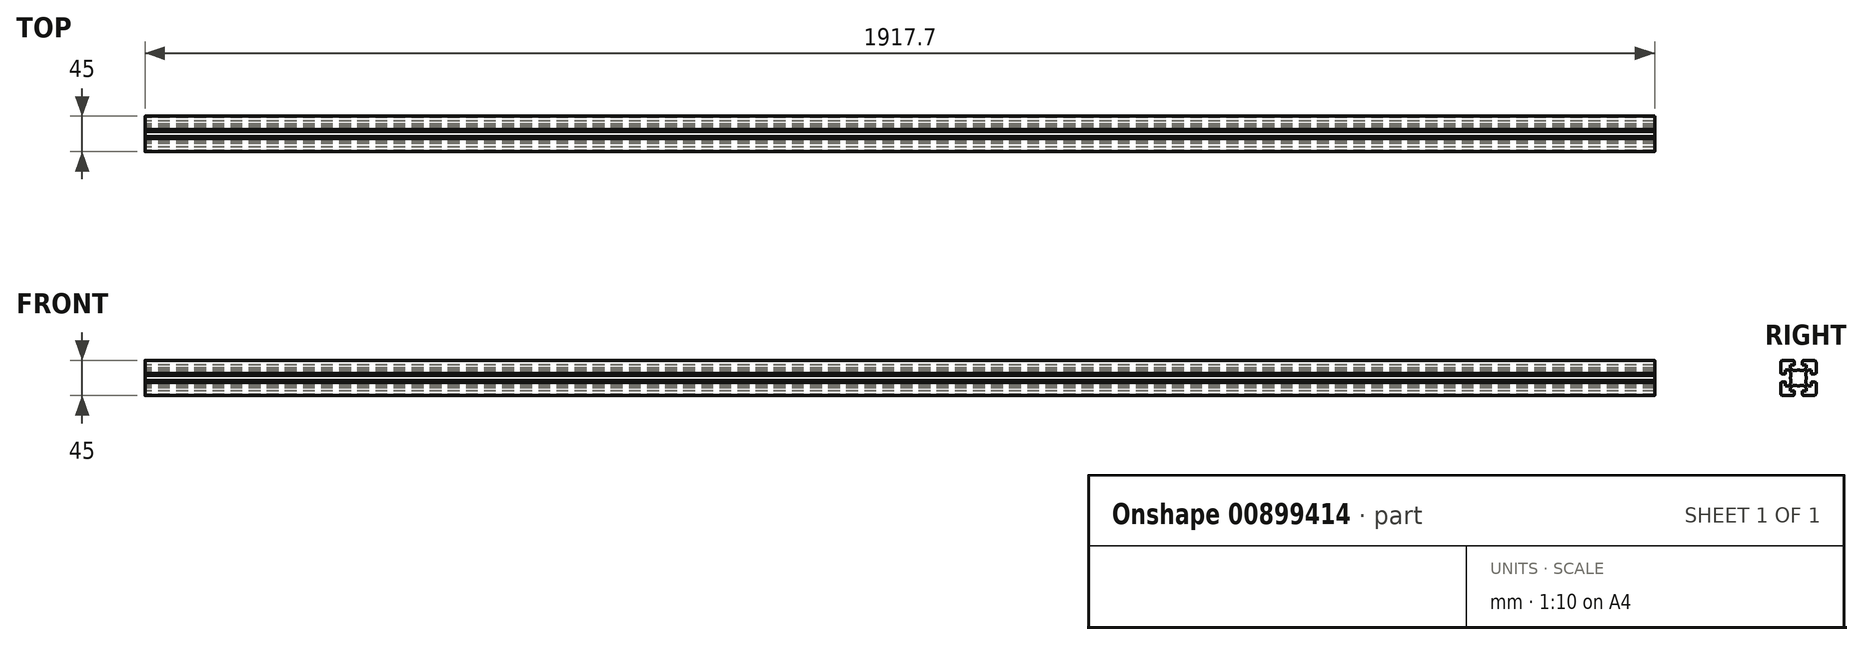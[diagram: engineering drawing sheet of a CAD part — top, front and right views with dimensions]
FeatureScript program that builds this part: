
annotation { "Feature Type Name" : "Feature", "Feature Type Description" : "" }
export const myFeature = defineFeature(function(context is Context, id is Id, definition is map)
    precondition{}
    {
        {
            var Q0;
            Q0=qCreatedBy(makeId("Right.planeOp"),FACE);
            var sketch = newSketch(context, id + "F0", { "sketchPlane" : qUnion([Q0])});
            skLineSegment(sketch, "E0", {"start": v(-20.09, -10.29) * mm, "end": v(-21.29, -10.29) * mm});
            skArc(sketch, "E1", {"start": v(-21.29, -10.29) * mm, "mid": v(-21.5, -10.38) * mm, "end": v(-21.59, -10.59) * mm});
            skLineSegment(sketch, "E2", {"start": v(-21.59, -10.59) * mm, "end": v(-21.59, -23.99) * mm});
            skArc(sketch, "E3", {"start": v(-21.59, -23.99) * mm, "mid": v(-20.7, -26.11) * mm, "end": v(-18.59, -26.99) * mm});
            skLineSegment(sketch, "E4", {"start": v(-18.59, -26.99) * mm, "end": v(-5.19, -26.99) * mm});
            skArc(sketch, "E5", {"start": v(-5.19, -26.99) * mm, "mid": v(-4.98, -26.9) * mm, "end": v(-4.89, -26.69) * mm});
            skLineSegment(sketch, "E6", {"start": v(-4.89, -26.69) * mm, "end": v(-4.89, -25.49) * mm});
            skLineSegment(sketch, "E7", {"start": v(-4.89, -25.49) * mm, "end": v(-4.39, -25.49) * mm});
            skArc(sketch, "E8", {"start": v(-4.39, -25.49) * mm, "mid": v(-4.18, -25.4) * mm, "end": v(-4.09, -25.19) * mm});
            skLineSegment(sketch, "E9", {"start": v(-4.09, -25.19) * mm, "end": v(-4.09, -21.29) * mm});
            skArc(sketch, "E10", {"start": v(-4.09, -21.29) * mm, "mid": v(-4.18, -21.08) * mm, "end": v(-4.39, -20.99) * mm});
            skLineSegment(sketch, "E11", {"start": v(-4.39, -20.99) * mm, "end": v(-9.14, -20.99) * mm});
            skLineSegment(sketch, "E12", {"start": v(-9.14, -20.99) * mm, "end": v(-9.14, -16.88) * mm});
            skLineSegment(sketch, "E13", {"start": v(-9.14, -16.88) * mm, "end": v(-6.25, -13.99) * mm});
            skLineSegment(sketch, "E14", {"start": v(-6.25, -13.99) * mm, "end": v(-2.21, -13.99) * mm});
            skArc(sketch, "E15", {"start": v(-2.21, -13.99) * mm, "mid": v(0.91, -14.49) * mm, "end": v(4.03, -13.99) * mm});
            skLineSegment(sketch, "E16", {"start": v(-20.09, -10.29) * mm, "end": v(-20.09, -9.79) * mm});
            skArc(sketch, "E17", {"start": v(-20.09, -9.79) * mm, "mid": v(-20, -9.58) * mm, "end": v(-19.79, -9.49) * mm});
            skLineSegment(sketch, "E18", {"start": v(-19.79, -9.49) * mm, "end": v(-15.89, -9.49) * mm});
            skArc(sketch, "E19", {"start": v(-15.89, -9.49) * mm, "mid": v(-15.68, -9.58) * mm, "end": v(-15.59, -9.79) * mm});
            skLineSegment(sketch, "E20", {"start": v(-15.59, -9.79) * mm, "end": v(-15.59, -14.54) * mm});
            skLineSegment(sketch, "E21", {"start": v(-15.59, -14.54) * mm, "end": v(-11.48, -14.54) * mm});
            skLineSegment(sketch, "E22", {"start": v(-11.48, -14.54) * mm, "end": v(-8.59, -11.65) * mm});
            skLineSegment(sketch, "E23", {"start": v(-8.59, -11.65) * mm, "end": v(-8.59, -7.61) * mm});
            skLineSegment(sketch, "E24", {"start": v(29.82, -4.49) * mm, "end": v(-31.05, -4.49) * mm});
            skLineSegment(sketch, "E25.MirrorCS", {"start": v(6.71, -25.49) * mm, "end": v(6.21, -25.49) * mm});
            skArc(sketch, "E26.MirrorCS", {"start": v(7.01, -26.99) * mm, "mid": v(6.8, -26.9) * mm, "end": v(6.71, -26.69) * mm});
            skLineSegment(sketch, "E27.MirrorCS", {"start": v(10.41, -11.65) * mm, "end": v(10.41, -7.61) * mm});
            skArc(sketch, "E28.MirrorCS", {"start": v(6.21, -25.49) * mm, "mid": v(6, -25.4) * mm, "end": v(5.91, -25.19) * mm});
            skLineSegment(sketch, "E29.MirrorCS", {"start": v(6.71, -26.69) * mm, "end": v(6.71, -25.49) * mm});
            skArc(sketch, "E30.MirrorCS", {"start": v(5.91, -21.29) * mm, "mid": v(6, -21.08) * mm, "end": v(6.21, -20.99) * mm});
            skLineSegment(sketch, "E31.MirrorCS", {"start": v(10.96, -16.88) * mm, "end": v(8.07, -13.99) * mm});
            skLineSegment(sketch, "E32.MirrorCS", {"start": v(13.3, -14.54) * mm, "end": v(10.41, -11.65) * mm});
            skLineSegment(sketch, "E33.MirrorCS", {"start": v(17.41, -14.54) * mm, "end": v(13.3, -14.54) * mm});
            skLineSegment(sketch, "E34.MirrorCS", {"start": v(17.41, -9.79) * mm, "end": v(17.41, -14.54) * mm});
            skLineSegment(sketch, "E35.MirrorCS", {"start": v(6.21, -20.99) * mm, "end": v(10.96, -20.99) * mm});
            skLineSegment(sketch, "E36.MirrorCS", {"start": v(8.07, -13.99) * mm, "end": v(4.03, -13.99) * mm});
            skArc(sketch, "E37.MirrorCS", {"start": v(4.03, -13.99) * mm, "mid": v(0.91, -14.49) * mm, "end": v(-2.21, -13.99) * mm});
            skLineSegment(sketch, "E38.MirrorCS", {"start": v(10.96, -20.99) * mm, "end": v(10.96, -16.88) * mm});
            skLineSegment(sketch, "E39.MirrorCS", {"start": v(5.91, -25.19) * mm, "end": v(5.91, -21.29) * mm});
            skArc(sketch, "E40.MirrorCS", {"start": v(23.41, -23.99) * mm, "mid": v(22.53, -26.11) * mm, "end": v(20.41, -26.99) * mm});
            skLineSegment(sketch, "E41.MirrorCS", {"start": v(20.41, -26.99) * mm, "end": v(7.01, -26.99) * mm});
            skLineSegment(sketch, "E42.MirrorCS", {"start": v(23.41, -10.59) * mm, "end": v(23.41, -23.99) * mm});
            skArc(sketch, "E43.MirrorCS", {"start": v(17.71, -9.49) * mm, "mid": v(17.5, -9.58) * mm, "end": v(17.41, -9.79) * mm});
            skArc(sketch, "E44.MirrorCS", {"start": v(23.11, -10.29) * mm, "mid": v(23.32, -10.38) * mm, "end": v(23.41, -10.59) * mm});
            skLineSegment(sketch, "E45.MirrorCS", {"start": v(21.91, -10.29) * mm, "end": v(21.91, -9.79) * mm});
            skLineSegment(sketch, "E46.MirrorCS", {"start": v(21.91, -10.29) * mm, "end": v(23.11, -10.29) * mm});
            skArc(sketch, "E47.MirrorCS", {"start": v(21.91, -9.79) * mm, "mid": v(21.82, -9.58) * mm, "end": v(21.61, -9.49) * mm});
            skLineSegment(sketch, "E48.MirrorCS", {"start": v(21.61, -9.49) * mm, "end": v(17.71, -9.49) * mm});
            skLineSegment(sketch, "E49.MirrorCS", {"start": v(6.71, 16.51) * mm, "end": v(6.21, 16.51) * mm});
            skArc(sketch, "E50.MirrorCS", {"start": v(-4.39, 16.51) * mm, "mid": v(-4.18, 16.42) * mm, "end": v(-4.09, 16.21) * mm});
            skLineSegment(sketch, "E51.MirrorCS", {"start": v(-4.89, 16.51) * mm, "end": v(-4.39, 16.51) * mm});
            skArc(sketch, "E52.MirrorCS", {"start": v(5.91, 12.31) * mm, "mid": v(6, 12.1) * mm, "end": v(6.21, 12.01) * mm});
            skLineSegment(sketch, "E53.MirrorCS", {"start": v(6.71, 17.71) * mm, "end": v(6.71, 16.51) * mm});
            skLineSegment(sketch, "E54.MirrorCS", {"start": v(-4.89, 17.71) * mm, "end": v(-4.89, 16.51) * mm});
            skArc(sketch, "E55.MirrorCS", {"start": v(-5.19, 18.01) * mm, "mid": v(-4.98, 17.92) * mm, "end": v(-4.89, 17.71) * mm});
            skArc(sketch, "E56.MirrorCS", {"start": v(-4.09, 12.31) * mm, "mid": v(-4.18, 12.1) * mm, "end": v(-4.39, 12.01) * mm});
            skArc(sketch, "E57.MirrorCS", {"start": v(7.01, 18.01) * mm, "mid": v(6.8, 17.92) * mm, "end": v(6.71, 17.71) * mm});
            skArc(sketch, "E58.MirrorCS", {"start": v(6.21, 16.51) * mm, "mid": v(6, 16.42) * mm, "end": v(5.91, 16.21) * mm});
            skArc(sketch, "E59.MirrorCS", {"start": v(23.11, 1.31) * mm, "mid": v(23.32, 1.4) * mm, "end": v(23.41, 1.61) * mm});
            skLineSegment(sketch, "E60.MirrorCS", {"start": v(21.91, 1.31) * mm, "end": v(21.91, 0.81) * mm});
            skArc(sketch, "E61.MirrorCS", {"start": v(-15.89, 0.51) * mm, "mid": v(-15.68, 0.6) * mm, "end": v(-15.59, 0.81) * mm});
            skArc(sketch, "E62.MirrorCS", {"start": v(-21.29, 1.31) * mm, "mid": v(-21.5, 1.4) * mm, "end": v(-21.59, 1.61) * mm});
            skArc(sketch, "E63.MirrorCS", {"start": v(17.71, 0.51) * mm, "mid": v(17.5, 0.6) * mm, "end": v(17.41, 0.81) * mm});
            skArc(sketch, "E64.MirrorCS", {"start": v(21.91, 0.81) * mm, "mid": v(21.82, 0.6) * mm, "end": v(21.61, 0.51) * mm});
            skLineSegment(sketch, "E65.MirrorCS", {"start": v(21.91, 1.31) * mm, "end": v(23.11, 1.31) * mm});
            skArc(sketch, "E66.MirrorCS", {"start": v(14.31, 5.31) * mm, "mid": v(14.1, 5.4) * mm, "end": v(14.01, 5.61) * mm});
            skArc(sketch, "E67.MirrorCS", {"start": v(-20.09, 0.81) * mm, "mid": v(-20, 0.6) * mm, "end": v(-19.79, 0.51) * mm});
            skLineSegment(sketch, "E68.MirrorCS", {"start": v(-20.09, 1.31) * mm, "end": v(-21.29, 1.31) * mm});
            skLineSegment(sketch, "E69.MirrorCS", {"start": v(-20.09, 1.31) * mm, "end": v(-20.09, 0.81) * mm});
            skLineSegment(sketch, "E70.MirrorCS", {"start": v(8.07, 5.01) * mm, "end": v(4.03, 5.01) * mm});
            skLineSegment(sketch, "E71.MirrorCS", {"start": v(-4.09, 16.21) * mm, "end": v(-4.09, 12.31) * mm});
            skLineSegment(sketch, "E72.MirrorCS", {"start": v(-9.14, 12.01) * mm, "end": v(-9.14, 7.9) * mm});
            skLineSegment(sketch, "E73.MirrorCS", {"start": v(-15.59, 5.56) * mm, "end": v(-11.48, 5.56) * mm});
            skLineSegment(sketch, "E74.MirrorCS", {"start": v(-4.39, 12.01) * mm, "end": v(-9.14, 12.01) * mm});
            skLineSegment(sketch, "E75.MirrorCS", {"start": v(-9.14, 7.9) * mm, "end": v(-6.25, 5.01) * mm});
            skLineSegment(sketch, "E76.MirrorCS", {"start": v(10.96, 12.01) * mm, "end": v(10.96, 7.9) * mm});
            skArc(sketch, "E77.MirrorCS", {"start": v(-21.59, 15.01) * mm, "mid": v(-20.7, 17.13) * mm, "end": v(-18.59, 18.01) * mm});
            skLineSegment(sketch, "E78.MirrorCS", {"start": v(23.41, 1.61) * mm, "end": v(23.41, 15.01) * mm});
            skLineSegment(sketch, "E79.MirrorCS", {"start": v(13.3, 5.56) * mm, "end": v(10.41, 2.67) * mm});
            skLineSegment(sketch, "E80.MirrorCS", {"start": v(-8.59, 2.67) * mm, "end": v(-8.59, -1.37) * mm});
            skLineSegment(sketch, "E81.MirrorCS", {"start": v(-15.59, 0.81) * mm, "end": v(-15.59, 5.56) * mm});
            skLineSegment(sketch, "E82.MirrorCS", {"start": v(10.41, 2.67) * mm, "end": v(10.41, -1.37) * mm});
            skLineSegment(sketch, "E83.MirrorCS", {"start": v(-18.59, 18.01) * mm, "end": v(-5.19, 18.01) * mm});
            skLineSegment(sketch, "E84.MirrorCS", {"start": v(10.96, 7.9) * mm, "end": v(8.07, 5.01) * mm});
            skLineSegment(sketch, "E85.MirrorCS", {"start": v(17.41, 5.56) * mm, "end": v(13.3, 5.56) * mm});
            skArc(sketch, "E86.MirrorCS", {"start": v(23.41, 15.01) * mm, "mid": v(22.53, 17.13) * mm, "end": v(20.41, 18.01) * mm});
            skLineSegment(sketch, "E87.MirrorCS", {"start": v(5.91, 16.21) * mm, "end": v(5.91, 12.31) * mm});
            skLineSegment(sketch, "E88.MirrorCS", {"start": v(17.41, 0.81) * mm, "end": v(17.41, 5.56) * mm});
            skLineSegment(sketch, "E89.MirrorCS", {"start": v(-11.48, 5.56) * mm, "end": v(-8.59, 2.67) * mm});
            skLineSegment(sketch, "E90.MirrorCS", {"start": v(-6.25, 5.01) * mm, "end": v(-2.21, 5.01) * mm});
            skLineSegment(sketch, "E91.MirrorCS", {"start": v(-21.59, 1.61) * mm, "end": v(-21.59, 15.01) * mm});
            skArc(sketch, "E92.MirrorCS", {"start": v(4.03, 5.01) * mm, "mid": v(0.91, 5.51) * mm, "end": v(-2.21, 5.01) * mm});
            skLineSegment(sketch, "E93.MirrorCS", {"start": v(6.21, 12.01) * mm, "end": v(10.96, 12.01) * mm});
            skArc(sketch, "E94.MirrorCS", {"start": v(-2.21, 5.01) * mm, "mid": v(0.91, 5.51) * mm, "end": v(4.03, 5.01) * mm});
            skLineSegment(sketch, "E95.MirrorCS", {"start": v(20.41, 18.01) * mm, "end": v(7.01, 18.01) * mm});
            skLineSegment(sketch, "E96.MirrorCS", {"start": v(-19.79, 0.51) * mm, "end": v(-15.89, 0.51) * mm});
            skLineSegment(sketch, "E97.MirrorCS", {"start": v(21.61, 0.51) * mm, "end": v(17.71, 0.51) * mm});
            skLineSegment(sketch, "E98.MirrorCS", {"start": v(0.91, -27.65) * mm, "end": v(0.91, 19.82) * mm});
            skArc(sketch, "E99", {"start": v(-8.59, -1.37) * mm, "mid": v(-9.09, -4.49) * mm, "end": v(-8.59, -7.61) * mm});
            skArc(sketch, "E100", {"start": v(10.41, -7.61) * mm, "mid": v(10.91, -4.49) * mm, "end": v(10.41, -1.37) * mm});
            skSolve(sketch);
        }
        {
            var Q0;
            Q0=qSketchRegion(id+"F0",true);
            extrude(context, id + "F1", {"entities" : qUnion([Q0]), "depth" : 1917.7 * mm, "offsetDistance" : 25.4 * mm});
        }
    });
